# Revit family: 2059756 Sylvania Lighting Fixture MUSE II 97 4K L3 SSC01 BLK
name_source: partatom
category: Lighting Fixtures
revit_build: Autodesk Revit 2016 (Build: 20150220_1215(x64)
units: mm (PartAtom-declared; Revit-internal decimal feet)

## family parameters
Always vertical = No
Cut with Voids When Loaded = No
Light Source = No
Part Type = Normal
Room Calculation Point = No
Round Connector Dimension = Use Diameter
Shared = No
Work Plane-Based = Yes

## types (1)
- 2059756 MUSE II 97 4K L3 SSC01 BLK
    Accessory Material = Aluminum_Sylvania_Beacon_Black
    Apparent Load = 21 VA
    Assembly Code = D5020200
    Average Life - L80/B10 = >72000
    Beam Angle = 55.00°
    Beam Angle Comments = Adjustable 8° through to 55°
    Body Material = Aluminum_Sylvania_Beacon_Black
    CRI (Ra) = 97 typical with R9 at 90
    Catalog Number = 2059748 MUSE II 97 3K L3 CASM BLK-WB
    Default Elevation = 0 mm  [stored 0 ft]
    Description = Beacon Muse II is the latest addition to the innovative and award winning Beacon Muse spotlight range. Beacon Muse II boasts improved optical control and provides an exciting accent and display lighting tool that uses cutting-edge LED technology and ancient lens principles to create a fully adjustable spotlight. The unique soft-touch ring enables the end-user to manually adjust the beam to from a wide flood (55˚) down to a tight spot (8˚); without the need of any additional lenses or reflectors. Beacon Muse II boasts a super high CRI of 97 with the R9 value at 90 -ensuring vibrant reds - the ideal spotlight for museum, gallery and retail applications where a high quality of light is required. Available with trailing edge, on-board dimming potentiometer, DALI or Casambi Wireless dimming.
    Diameter = 80 mm  [stored 0.262467 ft]
    Diffuser Material = Glass_Sylvania_Beacon_Clear_3000K
    Dimmable = Casambi Wireless
    Energy Class = A++, A+, A
    IK Rating = IK02
    IP Rating = IP20
    Initial Color = 3000 K
    Initial Intensity = 1081 lm
    Lamp = Integrated LED
    Lamp Type = IES : 2059756-WB
    Light Loss Factor = 1
    Manufacturer = Feilo Sylvania
    Model = MUSE II 97 4K L3 SSC01 BLK
    Mount = 3 Circuit Track (Lytespan 3)
    Product Family = BEACON MUSE II
    Reflector Material = Aluminum_Sylvania_Beacon_Bright
    Track Adaptor Type = Lytespan 3 - Three Circuit Adaptor
    URL = 0
    Voltage = 240 V
    Voltage Comments = UNV (Universal Voltage; 220-240 Volt)

note: [stored X ft] marks values corroborated as IEEE doubles in the binary element streams (Revit-internal decimal feet)

## geometry (parser evidence)
native form markers: Sweep x8
freeform/imported geometry present (non-native)
